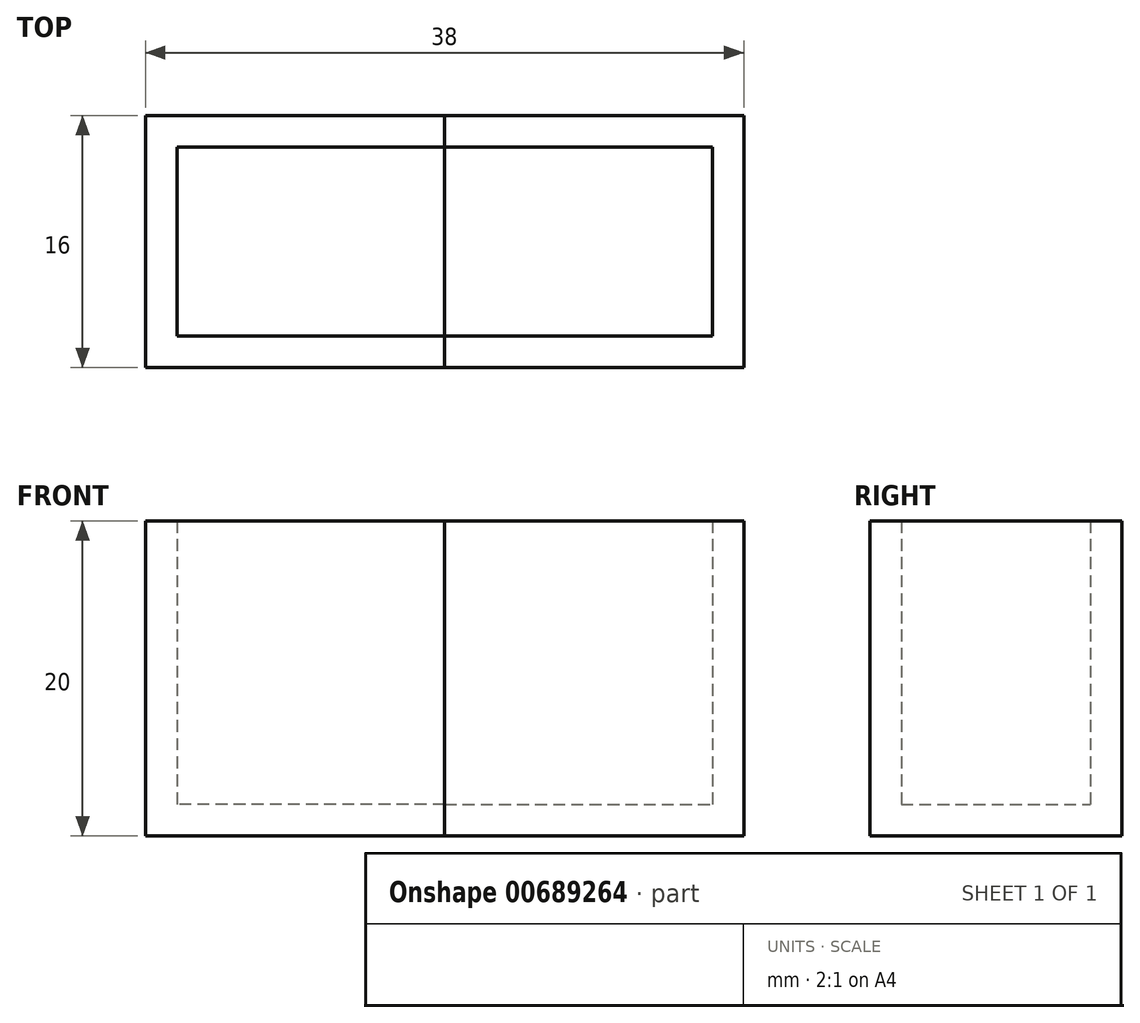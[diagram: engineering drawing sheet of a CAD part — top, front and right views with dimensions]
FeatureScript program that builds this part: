
annotation { "Feature Type Name" : "Feature", "Feature Type Description" : "" }
export const myFeature = defineFeature(function(context is Context, id is Id, definition is map)
    precondition{}
    {
        {
            var Q0;
            Q0=qCreatedBy(makeId("Top.planeOp"),FACE);
            var sketch = newSketch(context, id + "F0", { "sketchPlane" : qUnion([Q0])});
            skLineSegment(sketch, "E0.bottom", {"start": v(8.5, -6) * mm, "end": v(-8.5, -6) * mm});
            skLineSegment(sketch, "E0.top", {"start": v(8.5, 6) * mm, "end": v(-8.5, 6) * mm});
            skLineSegment(sketch, "E0.left", {"start": v(8.5, -6) * mm, "end": v(8.5, 6) * mm});
            skLineSegment(sketch, "E0.right", {"start": v(-8.5, -6) * mm, "end": v(-8.5, 6) * mm});
            skPoint(sketch, "E0.middle", {"position": v(0, 0) * mm});
            skLineSegment(sketch, "E1.bottom", {"start": v(-8.5, 8) * mm, "end": v(8.5, 8) * mm});
            skLineSegment(sketch, "E1.top", {"start": v(-8.5, 6) * mm, "end": v(8.5, 6) * mm});
            skLineSegment(sketch, "E1.left", {"start": v(-8.5, 8) * mm, "end": v(-8.5, 6) * mm});
            skLineSegment(sketch, "E1.right", {"start": v(8.5, 8) * mm, "end": v(8.5, 6) * mm});
            skLineSegment(sketch, "E2.MirrorCS", {"start": v(-8.5, -8) * mm, "end": v(8.5, -8) * mm});
            skLineSegment(sketch, "E3.MirrorCS", {"start": v(-8.5, -8) * mm, "end": v(-8.5, -6) * mm});
            skLineSegment(sketch, "E4.MirrorCS", {"start": v(8.5, -8) * mm, "end": v(8.5, -6) * mm});
            skLineSegment(sketch, "E5.bottom", {"start": v(-8.5, 8) * mm, "end": v(-10.5, 8) * mm});
            skLineSegment(sketch, "E5.top", {"start": v(-8.5, -8) * mm, "end": v(-10.5, -8) * mm});
            skLineSegment(sketch, "E5.left", {"start": v(-8.5, 8) * mm, "end": v(-8.5, -8) * mm});
            skLineSegment(sketch, "E5.right", {"start": v(-10.5, 8) * mm, "end": v(-10.5, -8) * mm});
            skSolve(sketch);
        }
        {
            var Q0;
            {var subQ3=sQuery(id+"F0.wireOp",EDGE,"E5.bottom");Q0=makeQuery(id+"F0.imprint","IMPRINT",FACE,{"disambiguationData":[TD([[makeQuery(id+"F0.imprint","IMPRINT",EDGE,{"derivedFrom":subQ3}),1.0]])]});}
            var Q1;
            {var subQ0=sQuery(id+"F0.wireOp",EDGE,"E0.bottom");Q1=makeQuery(id+"F0.imprint","IMPRINT",FACE,{"disambiguationData":[TD([[makeQuery(id+"F0.imprint","IMPRINT",EDGE,{"derivedFrom":subQ0}),1.0]])]});}
            extrude(context, id + "F1", {"entities" : qUnion([Q0, Q1]), "depth" : 20 * mm, "offsetDistance" : 25 * mm});
        }
        {
            var Q0;
            {var subQ0=sQuery(id+"F0.wireOp",EDGE,"E0.bottom");Q0=makeQuery(id+"F0.imprint","IMPRINT",FACE,{"disambiguationData":[TD([[makeQuery(id+"F0.imprint","IMPRINT",EDGE,{"derivedFrom":subQ0}),-1.0]])]});}
            extrude(context, id + "F2", {"entities" : qUnion([Q0]), "operationType" : NewBodyOperationType.ADD, "depth" : 2 * mm, "offsetDistance" : 25 * mm});
        }
        {
            var Q0;
            {var subQ0=sQuery(id+"F0.wireOp",EDGE,"E1.bottom");Q0=makeQuery(id+"F0.imprint","IMPRINT",FACE,{"disambiguationData":[TD([[makeQuery(id+"F0.imprint","IMPRINT",EDGE,{"derivedFrom":subQ0}),-1.0]])]});}
            extrude(context, id + "F3", {"entities" : qUnion([Q0]), "operationType" : NewBodyOperationType.ADD, "flatOperationType" : FlatOperationType.REMOVE, "depth" : 20 * mm, "offsetDistance" : 25 * mm, "domain" : OperationDomain.MODEL});
        }
        {
            var Q0;
            Q0=makeQuery(id+"F1.opExtrude","SWEPT_BODY",BODY,{"disambiguationData":[OSD([sQuery(id+"F0.wireOp",EDGE,"E0.bottom"),sQuery(id+"F0.wireOp",EDGE,"E2.MirrorCS"),sQuery(id+"F0.wireOp",EDGE,"E4.MirrorCS"),sQuery(id+"F0.wireOp",EDGE,"E5.bottom"),sQuery(id+"F0.wireOp",EDGE,"E5.top"),sQuery(id+"F0.wireOp",EDGE,"E5.left"),sQuery(id+"F0.wireOp",EDGE,"E5.right")])]});
            var Q1;
            Q1=makeQuery(id+"F3.boolean.opBoolean","MERGE",FACE,{"derivedFrom":[makeQuery(id+"F2.boolean.opBoolean","MERGE",FACE,{"derivedFrom":[makeQuery(id+"F1.opExtrude","SWEPT_FACE",FACE,{"disambiguationData":[OSD([sQuery(id+"F0.wireOp",EDGE,"E4.MirrorCS")])]}),makeQuery(id+"F2.opExtrude","SWEPT_FACE",FACE,{"disambiguationData":[OSD([sQuery(id+"F0.wireOp",EDGE,"E0.left")])]})]}),makeQuery(id+"F3.opExtrude","SWEPT_FACE",FACE,{"disambiguationData":[OSD([sQuery(id+"F0.wireOp",EDGE,"E1.right")])]})]});
            mirror(context, id + "F4", {"entities" : qUnion([Q0]), "mirrorPlane" : qUnion([Q1])});
        }
    });
